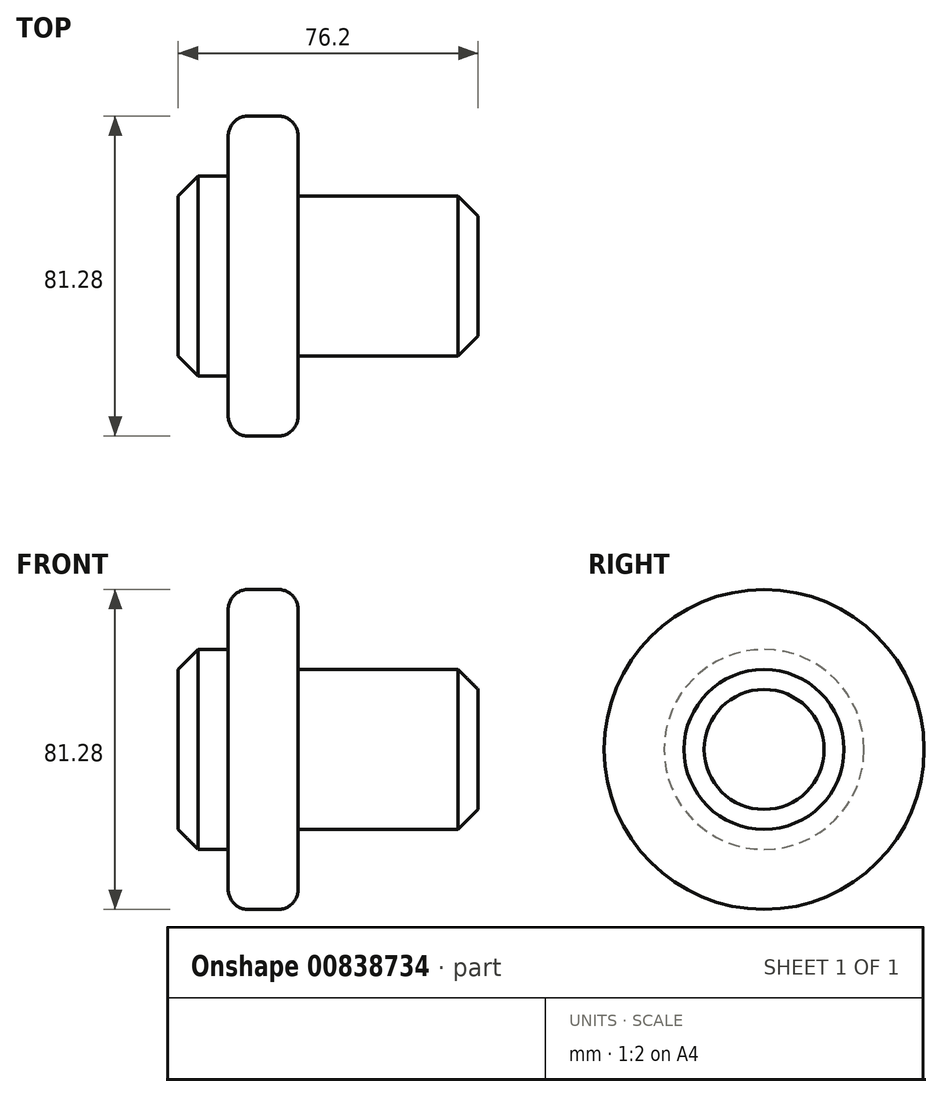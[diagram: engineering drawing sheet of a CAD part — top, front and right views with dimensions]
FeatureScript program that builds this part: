
annotation { "Feature Type Name" : "Feature", "Feature Type Description" : "" }
export const myFeature = defineFeature(function(context is Context, id is Id, definition is map)
    precondition{}
    {
        {
            var Q0;
            Q0=qCreatedBy(makeId("Top.planeOp"),FACE);
            var sketch = newSketch(context, id + "F0", { "sketchPlane" : qUnion([Q0])});
            skLineSegment(sketch, "E0", {"start": v(0, 0) * mm, "end": v(0, 25.4) * mm});
            skLineSegment(sketch, "E1", {"start": v(12.7, 25.4) * mm, "end": v(12.7, 40.64) * mm});
            skLineSegment(sketch, "E2", {"start": v(12.7, 40.64) * mm, "end": v(30.48, 40.64) * mm});
            skLineSegment(sketch, "E3", {"start": v(30.48, 40.64) * mm, "end": v(30.48, 20.32) * mm});
            skLineSegment(sketch, "E4", {"start": v(30.48, 20.32) * mm, "end": v(76.2, 20.32) * mm});
            skLineSegment(sketch, "E5", {"start": v(76.2, 20.32) * mm, "end": v(76.2, 0) * mm});
            skLineSegment(sketch, "E6", {"start": v(76.2, 0) * mm, "end": v(0, 0) * mm});
            skLineSegment(sketch, "E7", {"start": v(0, 25.4) * mm, "end": v(12.7, 25.4) * mm});
            skSolve(sketch);
        }
        {
            var Q0;
            Q0=makeQuery(id+"F0.imprint","IMPRINT",FACE,{"disambiguationData":[TD([[makeQuery(id+"F0.imprint","IMPRINT",EDGE,{"derivedFrom":sQuery(id+"F0.wireOp",EDGE,"E0")}),-1.0]])]});
            var Q1;
            Q1=sQuery(id+"F0.wireOp",EDGE,"E6");
            revolve(context, id + "F1", {"surfaceOperationType" : NewSurfaceOperationType.NEW, "entities" : qUnion([Q0]), "axis" : qUnion([Q1]), "revolveType" : RevolveType.FULL});
        }
        {
            var Q0;
            Q0=makeQuery(id+"F1.opRevolve","SWEPT_EDGE",EDGE,{"disambiguationData":[OSD([sQuery(id+"F0.wireOp",EDGE,"E4"),sQuery(id+"F0.wireOp",EDGE,"E5")])]});
            chamfer(context, id + "F2", {"entities" : qUnion([Q0]), "chamferType" : ChamferType.OFFSET_ANGLE, "width" : 5.08 * mm, "oppositeDirection" : false, "angle" : 45 * degree, "tangentPropagation" : true});
        }
        {
            var Q0;
            Q0=makeQuery(id+"F1.opRevolve","SWEPT_EDGE",EDGE,{"disambiguationData":[OSD([sQuery(id+"F0.wireOp",EDGE,"E1"),sQuery(id+"F0.wireOp",EDGE,"E2")])]});
            var Q1;
            Q1=makeQuery(id+"F1.opRevolve","SWEPT_EDGE",EDGE,{"disambiguationData":[OSD([sQuery(id+"F0.wireOp",EDGE,"E2"),sQuery(id+"F0.wireOp",EDGE,"E3")])]});
            fillet(context, id + "F3", {"entities" : qUnion([Q0, Q1]), "radius" : 5.08 * mm, "tangentPropagation" : true, "allowEdgeOverflow" : false});
        }
        {
            var Q0;
            Q0=makeQuery(id+"F1.opRevolve","SWEPT_EDGE",EDGE,{"disambiguationData":[OSD([sQuery(id+"F0.wireOp",EDGE,"E0"),sQuery(id+"F0.wireOp",EDGE,"E7")])]});
            chamfer(context, id + "F4", {"entities" : qUnion([Q0]), "width" : 5.08 * mm, "tangentPropagation" : true});
        }
    });
